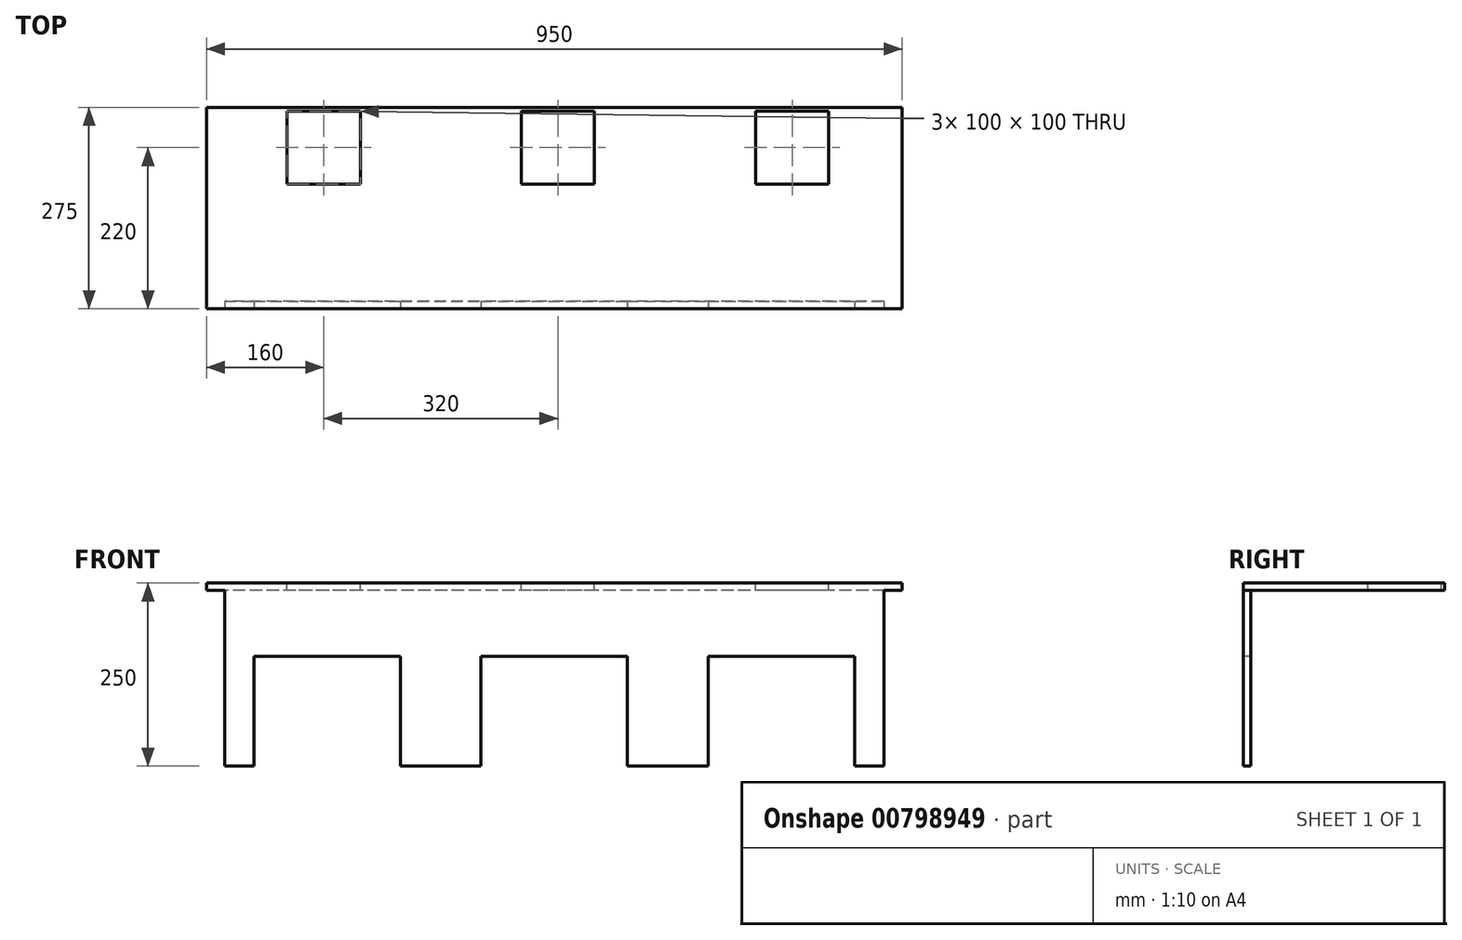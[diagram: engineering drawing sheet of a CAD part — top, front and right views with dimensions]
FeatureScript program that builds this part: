
annotation { "Feature Type Name" : "Feature", "Feature Type Description" : "" }
export const myFeature = defineFeature(function(context is Context, id is Id, definition is map)
    precondition{}
    {
        {
            var Q0;
            Q0=qCreatedBy(makeId("Top.planeOp"),FACE);
            var sketch = newSketch(context, id + "F0", { "sketchPlane" : qUnion([Q0])});
            skLineSegment(sketch, "E0.bottom", {"start": v(475, -137.5) * mm, "end": v(-475, -137.5) * mm});
            skLineSegment(sketch, "E0.top", {"start": v(475, 137.5) * mm, "end": v(-475, 137.5) * mm});
            skLineSegment(sketch, "E0.left", {"start": v(475, -137.5) * mm, "end": v(475, 137.5) * mm});
            skLineSegment(sketch, "E0.right", {"start": v(-475, -137.5) * mm, "end": v(-475, 137.5) * mm});
            skPoint(sketch, "E0.middle", {"position": v(0, 0) * mm});
            skSolve(sketch);
        }
        {
            var Q0;
            Q0=makeQuery(id+"F0.imprint","IMPRINT",FACE,{"disambiguationData":[TD([[makeQuery(id+"F0.imprint","IMPRINT",EDGE,{"derivedFrom":sQuery(id+"F0.wireOp",EDGE,"E0.bottom")}),-1.0]])]});
            extrude(context, id + "F1", {"entities" : qUnion([Q0]), "depth" : 10 * mm, "offsetDistance" : 25 * mm});
        }
        {
            var Q0;
            Q0=makeQuery(id+"F1.opExtrude","SWEPT_FACE",FACE,{"disambiguationData":[OSD([sQuery(id+"F0.wireOp",EDGE,"E0.bottom")])]});
            var sketch = newSketch(context, id + "F2", { "sketchPlane" : qUnion([Q0])});
            skLineSegment(sketch, "E1.bottom", {"start": v(-450, 0) * mm, "end": v(450, 0) * mm});
            skLineSegment(sketch, "E1.top", {"start": v(-450, -240) * mm, "end": v(450, -240) * mm});
            skLineSegment(sketch, "E1.left", {"start": v(-450, 0) * mm, "end": v(-450, -240) * mm});
            skLineSegment(sketch, "E1.right", {"start": v(450, 0) * mm, "end": v(450, -240) * mm});
            skSolve(sketch);
        }
        {
            var Q0;
            Q0=makeQuery(id+"F2.imprint","IMPRINT",FACE,{"disambiguationData":[TD([[makeQuery(id+"F2.imprint","IMPRINT",EDGE,{"derivedFrom":sQuery(id+"F2.wireOp",EDGE,"E1.bottom")}),1.0]])]});
            extrude(context, id + "F3", {"entities" : qUnion([Q0]), "operationType" : NewBodyOperationType.ADD, "oppositeDirection" : true, "depth" : 10 * mm, "offsetDistance" : 25 * mm});
        }
        {
            var Q0;
            Q0=makeQuery(id+"F3.boolean.opBoolean","MERGE",FACE,{"derivedFrom":[makeQuery(id+"F1.opExtrude","SWEPT_FACE",FACE,{"disambiguationData":[OSD([sQuery(id+"F0.wireOp",EDGE,"E0.bottom")])]}),makeQuery(id+"F3.opExtrude","CAP_FACE",FACE,{"disambiguationData":[OSD([sQuery(id+"F2.wireOp",EDGE,"E1.bottom"),sQuery(id+"F2.wireOp",EDGE,"E1.top"),sQuery(id+"F2.wireOp",EDGE,"E1.left"),sQuery(id+"F2.wireOp",EDGE,"E1.right")])],"isStart":true})]});
            var sketch = newSketch(context, id + "F4", { "sketchPlane" : qUnion([Q0])});
            skLineSegment(sketch, "E2.bottom", {"start": v(-410, -240) * mm, "end": v(-210, -240) * mm});
            skLineSegment(sketch, "E2.top", {"start": v(-410, -90) * mm, "end": v(-210, -90) * mm});
            skLineSegment(sketch, "E2.left", {"start": v(-410, -240) * mm, "end": v(-410, -90) * mm});
            skLineSegment(sketch, "E2.right", {"start": v(-210, -240) * mm, "end": v(-210, -90) * mm});
            skLineSegment(sketch, "E3.bottom", {"start": v(-100, -240) * mm, "end": v(100, -240) * mm});
            skLineSegment(sketch, "E3.top", {"start": v(-100, -90) * mm, "end": v(100, -90) * mm});
            skLineSegment(sketch, "E3.left", {"start": v(-100, -240) * mm, "end": v(-100, -90) * mm});
            skLineSegment(sketch, "E3.right", {"start": v(100, -240) * mm, "end": v(100, -90) * mm});
            skLineSegment(sketch, "E4.bottom", {"start": v(210, -240) * mm, "end": v(410, -240) * mm});
            skLineSegment(sketch, "E4.top", {"start": v(210, -90) * mm, "end": v(410, -90) * mm});
            skLineSegment(sketch, "E4.left", {"start": v(210, -240) * mm, "end": v(210, -90) * mm});
            skLineSegment(sketch, "E4.right", {"start": v(410, -240) * mm, "end": v(410, -90) * mm});
            skSolve(sketch);
        }
        {
            var Q0;
            Q0=makeQuery(id+"F4.imprint","IMPRINT",FACE,{"disambiguationData":[TD([[makeQuery(id+"F4.imprint","IMPRINT",EDGE,{"derivedFrom":sQuery(id+"F4.wireOp",EDGE,"E2.bottom")}),1.0]])]});
            var Q1;
            Q1=makeQuery(id+"F4.imprint","IMPRINT",FACE,{"disambiguationData":[TD([[makeQuery(id+"F4.imprint","IMPRINT",EDGE,{"derivedFrom":sQuery(id+"F4.wireOp",EDGE,"E3.bottom")}),1.0]])]});
            var Q2;
            Q2=makeQuery(id+"F4.imprint","IMPRINT",FACE,{"disambiguationData":[TD([[makeQuery(id+"F4.imprint","IMPRINT",EDGE,{"derivedFrom":sQuery(id+"F4.wireOp",EDGE,"E4.bottom")}),1.0]])]});
            extrude(context, id + "F5", {"entities" : qUnion([Q0, Q1, Q2]), "operationType" : NewBodyOperationType.REMOVE, "oppositeDirection" : true, "depth" : 10 * mm, "offsetDistance" : 25 * mm});
        }
        {
            var Q0;
            Q0=makeQuery(id+"F1.opExtrude","CAP_FACE",FACE,{"disambiguationData":[OSD([sQuery(id+"F0.wireOp",EDGE,"E0.bottom"),sQuery(id+"F0.wireOp",EDGE,"E0.top"),sQuery(id+"F0.wireOp",EDGE,"E0.left"),sQuery(id+"F0.wireOp",EDGE,"E0.right")])],"isStart":false});
            var sketch = newSketch(context, id + "F6", { "sketchPlane" : qUnion([Q0])});
            skLineSegment(sketch, "E5", {"start": v(-475, 132.5) * mm, "end": v(475, 132.5) * mm, "construction": true});
            skLineSegment(sketch, "E6", {"start": v(-475, 32.5) * mm, "end": v(475, 32.5) * mm, "construction": true});
            skLineSegment(sketch, "E7.bottom", {"start": v(375, 132.5) * mm, "end": v(275, 132.5) * mm});
            skLineSegment(sketch, "E7.top", {"start": v(375, 32.5) * mm, "end": v(275, 32.5) * mm});
            skLineSegment(sketch, "E7.left", {"start": v(375, 132.5) * mm, "end": v(375, 32.5) * mm});
            skLineSegment(sketch, "E7.right", {"start": v(275, 132.5) * mm, "end": v(275, 32.5) * mm});
            skLineSegment(sketch, "E8.bottom", {"start": v(55, 132.5) * mm, "end": v(-45, 132.5) * mm});
            skLineSegment(sketch, "E8.top", {"start": v(55, 32.5) * mm, "end": v(-45, 32.5) * mm});
            skLineSegment(sketch, "E8.left", {"start": v(55, 132.5) * mm, "end": v(55, 32.5) * mm});
            skLineSegment(sketch, "E8.right", {"start": v(-45, 132.5) * mm, "end": v(-45, 32.5) * mm});
            skLineSegment(sketch, "E9.bottom", {"start": v(-265, 132.5) * mm, "end": v(-365, 132.5) * mm});
            skLineSegment(sketch, "E9.top", {"start": v(-265, 32.5) * mm, "end": v(-365, 32.5) * mm});
            skLineSegment(sketch, "E9.left", {"start": v(-265, 132.5) * mm, "end": v(-265, 32.5) * mm});
            skLineSegment(sketch, "E9.right", {"start": v(-365, 132.5) * mm, "end": v(-365, 32.5) * mm});
            skLineSegment(sketch, "E10.bottom", {"start": v(-410.08, 132.5) * mm, "end": v(-510.08, 132.5) * mm});
            skLineSegment(sketch, "E10.top", {"start": v(-410.08, 32.5) * mm, "end": v(-510.08, 32.5) * mm});
            skLineSegment(sketch, "E10.left", {"start": v(-410.08, 132.5) * mm, "end": v(-410.08, 32.5) * mm});
            skLineSegment(sketch, "E10.right", {"start": v(-510.08, 132.5) * mm, "end": v(-510.08, 32.5) * mm});
            skSolve(sketch);
        }
        {
            var Q0;
            Q0=makeQuery(id+"F6.imprint","IMPRINT",FACE,{"disambiguationData":[TD([[makeQuery(id+"F6.imprint","IMPRINT",EDGE,{"derivedFrom":sQuery(id+"F6.wireOp",EDGE,"E9.bottom")}),1.0]])]});
            var Q1;
            Q1=makeQuery(id+"F6.imprint","IMPRINT",FACE,{"disambiguationData":[TD([[makeQuery(id+"F6.imprint","IMPRINT",EDGE,{"derivedFrom":sQuery(id+"F6.wireOp",EDGE,"E8.bottom")}),1.0]])]});
            var Q2;
            Q2=makeQuery(id+"F6.imprint","IMPRINT",FACE,{"disambiguationData":[TD([[makeQuery(id+"F6.imprint","IMPRINT",EDGE,{"derivedFrom":sQuery(id+"F6.wireOp",EDGE,"E7.bottom")}),1.0]])]});
            extrude(context, id + "F7", {"entities" : qUnion([Q0, Q1, Q2]), "operationType" : NewBodyOperationType.REMOVE, "oppositeDirection" : true, "depth" : 10 * mm, "offsetDistance" : 25 * mm});
        }
    });
